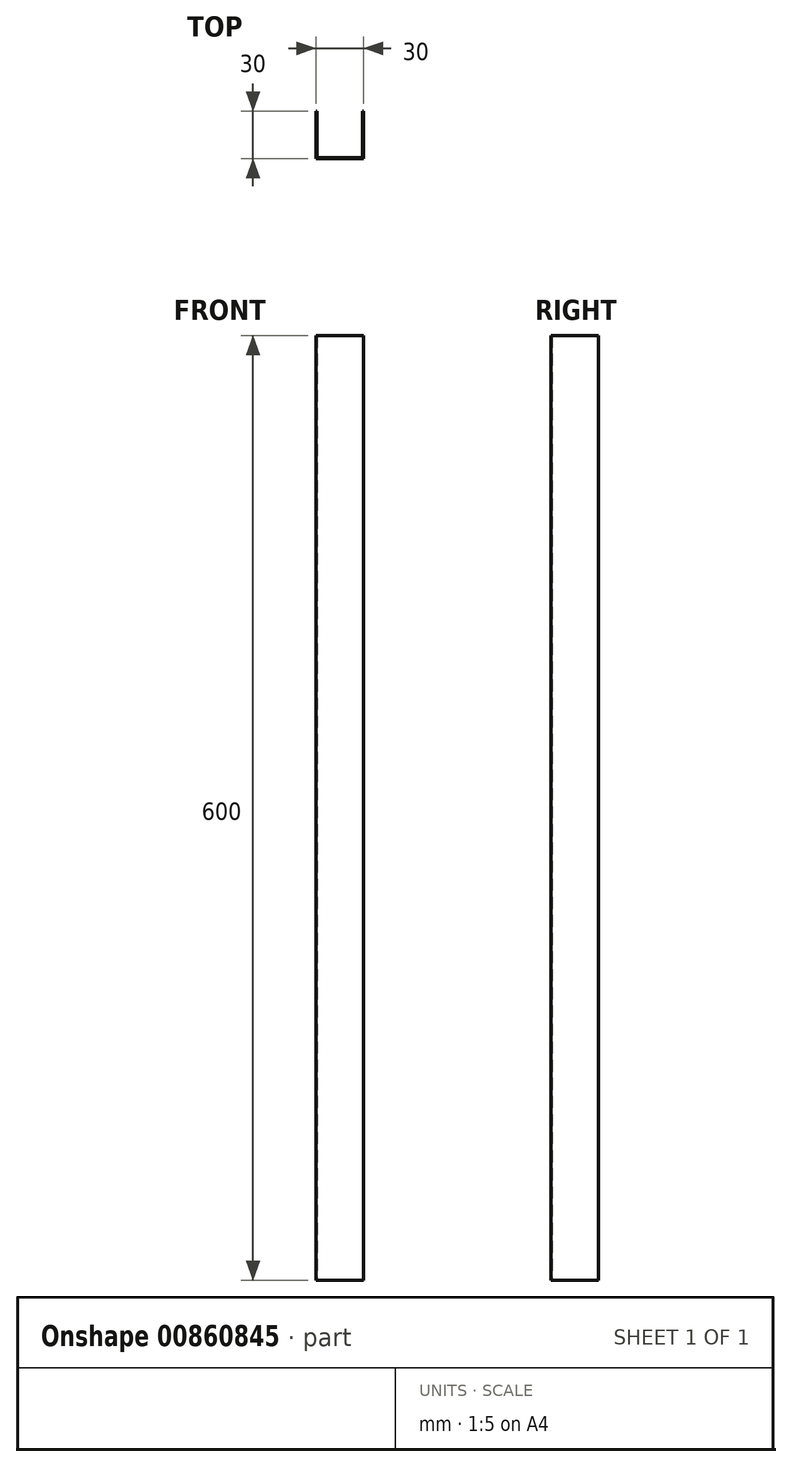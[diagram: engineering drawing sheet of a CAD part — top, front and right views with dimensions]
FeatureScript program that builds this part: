
annotation { "Feature Type Name" : "Feature", "Feature Type Description" : "" }
export const myFeature = defineFeature(function(context is Context, id is Id, definition is map)
    precondition{}
    {
        {
            var Q0;
            Q0=qCreatedBy(makeId("Top.planeOp"),FACE);
            var sketch = newSketch(context, id + "F0", { "sketchPlane" : qUnion([Q0])});
            skLineSegment(sketch, "E0.bottom", {"start": v(0.82, -17.94) * mm, "end": v(30.82, -17.94) * mm});
            skLineSegment(sketch, "E0.top", {"start": v(0.82, -18.44) * mm, "end": v(30.82, -18.44) * mm});
            skLineSegment(sketch, "E0.left", {"start": v(0.82, -17.94) * mm, "end": v(0.82, -18.44) * mm});
            skLineSegment(sketch, "E0.right", {"start": v(30.82, -17.94) * mm, "end": v(30.82, -18.44) * mm});
            skLineSegment(sketch, "E1.bottom", {"start": v(0.82, -18.44) * mm, "end": v(1.32, -18.44) * mm});
            skLineSegment(sketch, "E1.top", {"start": v(0.82, 11.56) * mm, "end": v(1.32, 11.56) * mm});
            skLineSegment(sketch, "E1.left", {"start": v(0.82, -18.44) * mm, "end": v(0.82, 11.56) * mm});
            skLineSegment(sketch, "E1.right", {"start": v(1.32, -18.44) * mm, "end": v(1.32, 11.56) * mm});
            skLineSegment(sketch, "E2.bottom", {"start": v(30.82, -18.44) * mm, "end": v(30.32, -18.44) * mm});
            skLineSegment(sketch, "E2.top", {"start": v(30.82, 11.56) * mm, "end": v(30.32, 11.56) * mm});
            skLineSegment(sketch, "E2.left", {"start": v(30.82, -18.44) * mm, "end": v(30.82, 11.56) * mm});
            skLineSegment(sketch, "E2.right", {"start": v(30.32, -18.44) * mm, "end": v(30.32, 11.56) * mm});
            skSolve(sketch);
        }
        {
            var Q0;
            {var subQ4=sQuery(id+"F0.wireOp",EDGE,"E1.top");Q0=makeQuery(id+"F0.imprint","IMPRINT",FACE,{"disambiguationData":[TD([[makeQuery(id+"F0.imprint","IMPRINT",EDGE,{"derivedFrom":subQ4}),-1.0]])]});}
            var Q1;
            {var subQ0=sQuery(id+"F0.wireOp",EDGE,"E1.right");var subQ1=sQuery(id+"F0.wireOp",EDGE,"E0.bottom");var subQ2=makeQuery(id+"F0.imprint","INTERSECT",VERTEX,{"derivedFrom":[subQ1,subQ0]});Q1=makeQuery(id+"F0.imprint","IMPRINT",FACE,{"disambiguationData":[TD([[makeQuery(id+"F0.imprint","IMPRINT",EDGE,{"disambiguationData":[TD([[subQ2,-1.0]])],"derivedFrom":subQ1}),-1.0]])]});}
            var Q2;
            {var subQ4=sQuery(id+"F0.wireOp",EDGE,"E2.top");Q2=makeQuery(id+"F0.imprint","IMPRINT",FACE,{"disambiguationData":[TD([[makeQuery(id+"F0.imprint","IMPRINT",EDGE,{"derivedFrom":subQ4}),1.0]])]});}
            var Q3;
            {var subQ0=sQuery(id+"F0.wireOp",EDGE,"E0.right");Q3=makeQuery(id+"F0.imprint","IMPRINT",FACE,{"disambiguationData":[TD([[makeQuery(id+"F0.imprint","IMPRINT",EDGE,{"derivedFrom":subQ0}),-1.0]])]});}
            var Q4;
            {var subQ3=sQuery(id+"F0.wireOp",EDGE,"E0.left");Q4=makeQuery(id+"F0.imprint","IMPRINT",FACE,{"disambiguationData":[TD([[makeQuery(id+"F0.imprint","IMPRINT",EDGE,{"derivedFrom":subQ3}),1.0]])]});}
            extrude(context, id + "F1", {"entities" : qUnion([Q0, Q1, Q2, Q3, Q4]), "depth" : 600 * mm, "offsetDistance" : 25 * mm});
        }
    });
